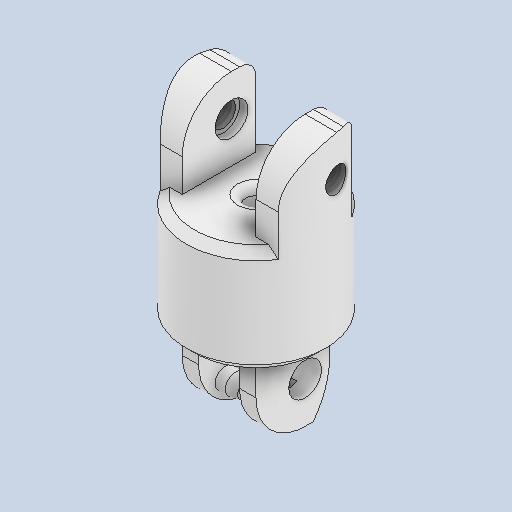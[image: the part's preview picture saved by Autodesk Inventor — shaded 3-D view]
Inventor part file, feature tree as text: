
AUTODESK INVENTOR PART (.ipt)
format: ipt  version: 2022 (Build 260153000, 153)  size: 273,408 bytes
history: native  units: in
note: dims shown in document units (in); Inventor stores cm internally (conversion verified against a paired STEP export)
features: sketch x10, extrude x7, fillet x6, chamfer x4, hole x3, thread x2
ambient origin geometry x8: Origin, YZ Plane, XZ Plane, XY Plane, X Axis, Y Axis, Z Axis, Center Point
bodies: Solid1 (feature_tree)
feature tree (32):
  extrude  "Extrusion1"  Depth=0.3937in
  extrude  "Extrusion2"  Depth=0.0394in TaperAngle=0.0deg
  fillet  "Fillet4"  Radius=0.0394in
  fillet  "Fillet5"  Radius=0.2362in
  fillet  "Fillet6"  Radius=0.3937in
  hole  "Hole1"  [1 undecoded]
  extrude  "Extrusion3"  Depth=0.0492in TaperAngle=0.0deg
  chamfer  "Chamfer1"  Distance=0.0492in Angle=45.0deg
  extrude  "Extrusion4"  Depth=0.0394in TaperAngle=0.0deg
  chamfer  "Chamfer2"  Distance=0.3937in
  extrude  "Extrusion5"  Depth=0.0787in
  fillet  "Fillet8"  Radius=0.1969in
  fillet  "Fillet9"  Radius=0.1969in
  chamfer  "Chamfer3"  Distance=0.0394in Angle=45.0deg
  hole  "Hole2"  [1 undecoded]
  hole  "Hole3"  [1 undecoded]
  chamfer  "Chamfer4"  Distance=0.2362in
  fillet  "Fillet10"  [1 undecoded]
  thread  "Thread1"  [1 undecoded]
  thread  "Thread2"  [1 undecoded]
  sketch  "Sketch1"  dims[d8=0.3937in d9=0.0in d11=0.6693in]
  sketch  "Sketch2"  dims[d12=0.0984in d13=0.0394in d14=0.0in d19=0.0394in d22=0.2362in d23=0.3937in]
  sketch  "Sketch3"  dims[d24=0.1969in]
  sketch  "Sketch4"  dims[d25=0.1575in d26=0.2362in d27=0.1575in d28=0.0787in d29=90.0deg d30=0.3937in d31=0.0in d36=0.0984in d37=0.0in]
  sketch  "Sketch5"  dims[d38=0.0098in d39=0.0492in d40=45.0deg d41=0.0984in d42=0.0in d43=0.0098in d44=0.0492in d45=45.0deg]
  sketch  "Sketch6"  dims[d46=0.4331in d47=0.0in d48=0.0984in d49=0.6693in d51=0.0in d52=0.0394in d55=0.0in d56=0.3937in]
  sketch  "Sketch9"  dims[d63=0.1181in d64=0.2362in d65=0.1575in d66=0.0394in d67=90.0deg d68=0.1575in d69=0.0in d70=0.1969in]
  sketch  "Sketch10"  dims[d71=0.1181in d72=0.2362in d73=0.1575in d74=0.0394in d75=90.0deg d76=0.1575in d77=0.0in d78=0.0394in d79=0.0787in d80=45.0deg d81=0.0394in d82=0.2362in d83=0.0in d84=0.2362in d85=0.0in]
  sketch  "Sketch7"  dims[d57=0.2362in d58=0.0787in]
  sketch  "Sketch8"  dims[d59=0.0394in d60=0.0787in d61=45.0deg d62=0.1969in]
  extrude  "Extrusion6"  [1 undecoded]
  extrude  "Extrusion7"  [1 undecoded]
note: 8 required parameter values undecoded (feature->parameter linkage not recoverable at this tier; creation-order binding heuristic only, values carry confidence <= 0.55)
